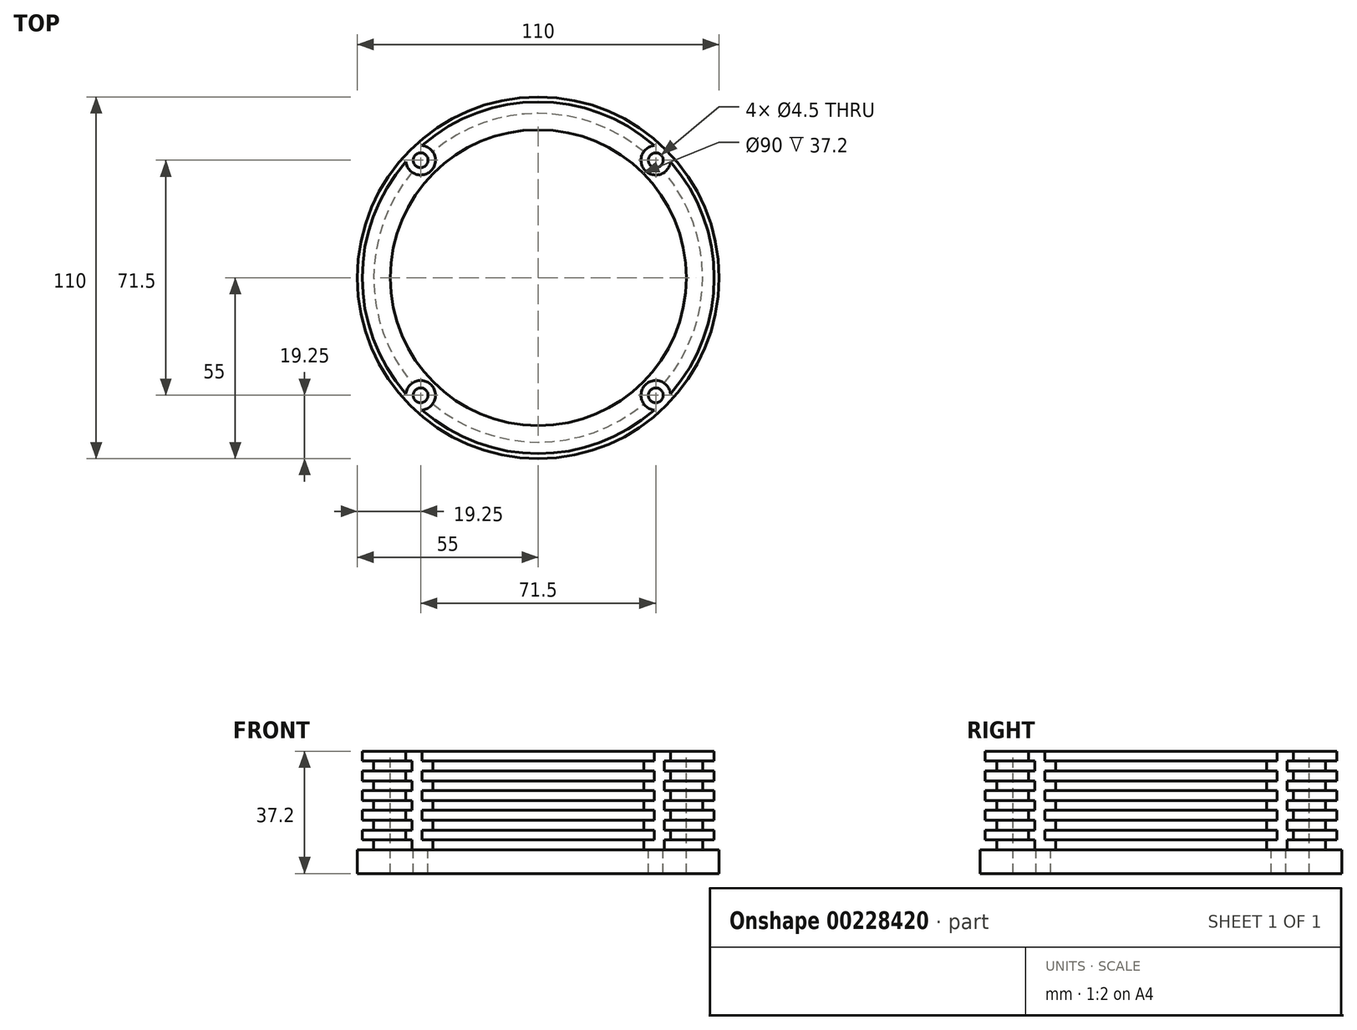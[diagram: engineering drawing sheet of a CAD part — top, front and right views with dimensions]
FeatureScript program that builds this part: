
annotation { "Feature Type Name" : "Feature", "Feature Type Description" : "" }
export const myFeature = defineFeature(function(context is Context, id is Id, definition is map)
    precondition{}
    {
        {
            var Q0;
            Q0=qCreatedBy(makeId("Top.planeOp"),FACE);
            var sketch = newSketch(context, id + "F0", { "sketchPlane" : qUnion([Q0])});
            skCircle(sketch, "E0", {"center": v(0, 0) * mm, "radius": 55 * mm});
            skSolve(sketch);
        }
        {
            var Q0;
            Q0=makeQuery(id+"F0.imprint","IMPRINT",FACE,{"disambiguationData":[TD([[makeQuery(id+"F0.imprint","IMPRINT",EDGE,{"derivedFrom":sQuery(id+"F0.wireOp",EDGE,"E0")}),1.0]])]});
            extrude(context, id + "F1", {"entities" : qUnion([Q0]), "depth" : 7.2 * mm});
        }
        {
            var Q0;
            Q0=makeQuery(id+"F1.opExtrude","CAP_FACE",FACE,{"disambiguationData":[OSD([sQuery(id+"F0.wireOp",EDGE,"E0")])],"isStart":false});
            var sketch = newSketch(context, id + "F2", { "sketchPlane" : qUnion([Q0])});
            skCircle(sketch, "E1", {"center": v(-35.75, 35.75) * mm, "radius": 2.25 * mm});
            skCircle(sketch, "E2.1.0", {"center": v(-35.75, -35.75) * mm, "radius": 2.25 * mm});
            skCircle(sketch, "E2.2.0", {"center": v(35.75, -35.75) * mm, "radius": 2.25 * mm});
            skCircle(sketch, "E2.3.0", {"center": v(35.75, 35.75) * mm, "radius": 2.25 * mm});
            skPoint(sketch, "E2.center", {"position": v(0, 0) * mm});
            skSolve(sketch);
        }
        {
            var Q0;
            Q0=qCreatedBy(makeId("Front.planeOp"),FACE);
            var sketch = newSketch(context, id + "F3", { "sketchPlane" : qUnion([Q0])});
            skLineSegment(sketch, "E3.top", {"start": v(0, 7.2) * mm, "end": v(53.5, 7.2) * mm});
            skLineSegment(sketch, "E3.left", {"start": v(0, 37.2) * mm, "end": v(0, 7.2) * mm});
            skLineSegment(sketch, "E4", {"start": v(53.5, 37.2) * mm, "end": v(53.5, 34.2) * mm});
            skLineSegment(sketch, "E5", {"start": v(53.5, 34.2) * mm, "end": v(50, 34.2) * mm});
            skLineSegment(sketch, "E6", {"start": v(50, 34.2) * mm, "end": v(50, 31.2) * mm});
            skLineSegment(sketch, "E7", {"start": v(50, 31.2) * mm, "end": v(53.5, 31.2) * mm});
            skLineSegment(sketch, "E8", {"start": v(53.5, 31.2) * mm, "end": v(53.5, 28.2) * mm});
            skLineSegment(sketch, "E9", {"start": v(53.5, 28.2) * mm, "end": v(50, 28.2) * mm});
            skLineSegment(sketch, "E10", {"start": v(50, 28.2) * mm, "end": v(50, 25.2) * mm});
            skLineSegment(sketch, "E11", {"start": v(50, 25.2) * mm, "end": v(53.5, 25.2) * mm});
            skLineSegment(sketch, "E12", {"start": v(53.5, 25.2) * mm, "end": v(53.5, 22.2) * mm});
            skLineSegment(sketch, "E13", {"start": v(53.5, 22.2) * mm, "end": v(50, 22.2) * mm});
            skLineSegment(sketch, "E14", {"start": v(50, 22.2) * mm, "end": v(50, 19.2) * mm});
            skLineSegment(sketch, "E15", {"start": v(50, 19.2) * mm, "end": v(53.5, 19.2) * mm});
            skLineSegment(sketch, "E16", {"start": v(53.5, 19.2) * mm, "end": v(53.5, 16.2) * mm});
            skLineSegment(sketch, "E17", {"start": v(53.5, 16.2) * mm, "end": v(50, 16.2) * mm});
            skLineSegment(sketch, "E18", {"start": v(50, 16.2) * mm, "end": v(50, 13.2) * mm});
            skLineSegment(sketch, "E19", {"start": v(50, 13.2) * mm, "end": v(53.5, 13.2) * mm});
            skLineSegment(sketch, "E20", {"start": v(53.5, 13.2) * mm, "end": v(53.5, 10.2) * mm});
            skLineSegment(sketch, "E21", {"start": v(53.5, 10.2) * mm, "end": v(50, 10.2) * mm});
            skLineSegment(sketch, "E22", {"start": v(53.5, 37.2) * mm, "end": v(0, 37.2) * mm});
            skLineSegment(sketch, "E23", {"start": v(50, 10.2) * mm, "end": v(50, 7.2) * mm});
            skSolve(sketch);
        }
        {
            var Q0;
            {var subQ0=sQuery(id+"F3.wireOp",EDGE,"E3.left");Q0=makeQuery(id+"F3.imprint","IMPRINT",FACE,{"disambiguationData":[TD([[makeQuery(id+"F3.imprint","IMPRINT",EDGE,{"derivedFrom":subQ0}),1.0]])]});}
            var Q1;
            Q1=sQuery(id+"F3.wireOp",EDGE,"E3.left");
            revolve(context, id + "F4", {"operationType" : NewBodyOperationType.ADD, "entities" : qUnion([Q0]), "axis" : qUnion([Q1]), "revolveType" : RevolveType.FULL});
        }
        {
            var Q0;
            Q0 = qSketchRegion(id + "F2", true);
            var Q1;
            Q1=makeQuery(id+"F1.opExtrude","SWEPT_BODY",BODY,{"disambiguationData":[OSD([sQuery(id+"F0.wireOp",EDGE,"E0")])]});
            extrude(context, id + "F5", {"entities" : qUnion([Q0]), "operationType" : NewBodyOperationType.REMOVE, "endBound" : BoundingType.UP_TO_BODY, "oppositeDirection" : true, "endBoundEntityBody" : qUnion([Q1]), "depth" : 25 * mm});
        }
        {
            var Q0;
            Q0=makeQuery(id+"F4.opRevolve","SWEPT_FACE",FACE,{"disambiguationData":[OSD([sQuery(id+"F3.wireOp",EDGE,"E22")])]});
            var sketch = newSketch(context, id + "F6", { "sketchPlane" : qUnion([Q0])});
            skCircle(sketch, "E24", {"center": v(-35.75, 35.75) * mm, "radius": 4.5 * mm});
            skCircle(sketch, "E25.1.0", {"center": v(-35.75, -35.75) * mm, "radius": 4.5 * mm});
            skCircle(sketch, "E25.2.0", {"center": v(35.75, -35.75) * mm, "radius": 4.5 * mm});
            skCircle(sketch, "E25.3.0", {"center": v(35.75, 35.75) * mm, "radius": 4.5 * mm});
            skPoint(sketch, "E25.center", {"position": v(0, 0) * mm});
            skSolve(sketch);
        }
        {
            var Q0;
            Q0 = qSketchRegion(id + "F6", true);
            var Q1;
            Q1=makeQuery(id+"F1.opExtrude","CAP_FACE",FACE,{"disambiguationData":[OSD([sQuery(id+"F0.wireOp",EDGE,"E0")])],"isStart":false});
            extrude(context, id + "F7", {"entities" : qUnion([Q0]), "operationType" : NewBodyOperationType.REMOVE, "endBound" : BoundingType.UP_TO_SURFACE, "oppositeDirection" : true, "endBoundEntityFace" : qUnion([Q1]), "depth" : 25 * mm});
        }
        {
            var Q0;
            Q0=makeQuery(id+"F4.opRevolve","SWEPT_FACE",FACE,{"disambiguationData":[OSD([sQuery(id+"F3.wireOp",EDGE,"E22")])]});
            var sketch = newSketch(context, id + "F8", { "sketchPlane" : qUnion([Q0])});
            skCircle(sketch, "E26", {"center": v(0, 0) * mm, "radius": 45 * mm});
            skSolve(sketch);
        }
        {
            var Q0;
            Q0=makeQuery(id+"F8.imprint","IMPRINT",FACE,{"disambiguationData":[TD([[makeQuery(id+"F8.imprint","IMPRINT",EDGE,{"derivedFrom":sQuery(id+"F8.wireOp",EDGE,"E26")}),1.0]])]});
            extrude(context, id + "F9", {"entities" : qUnion([Q0]), "operationType" : NewBodyOperationType.REMOVE, "endBound" : BoundingType.THROUGH_ALL, "oppositeDirection" : true, "depth" : 25 * mm});
        }
    });
